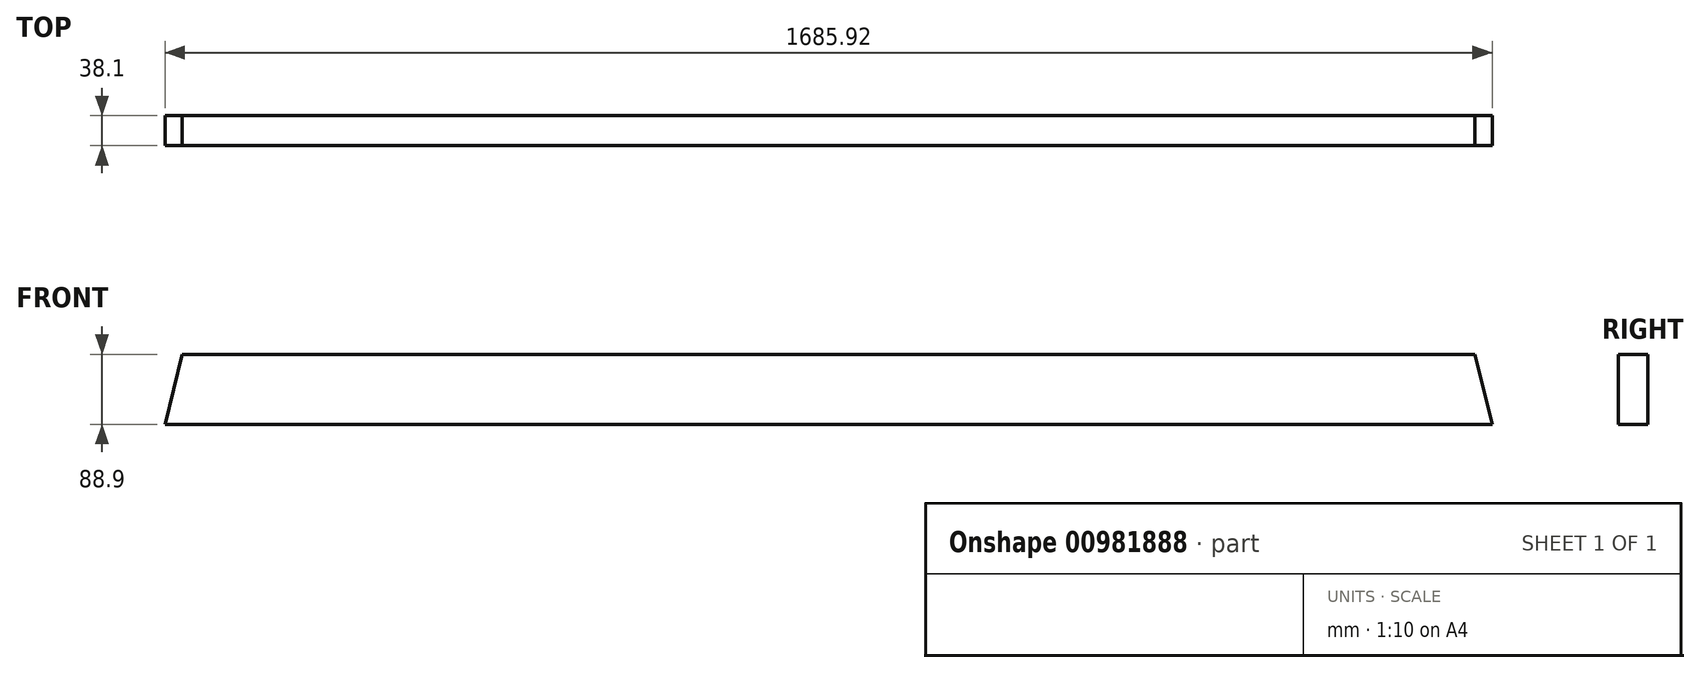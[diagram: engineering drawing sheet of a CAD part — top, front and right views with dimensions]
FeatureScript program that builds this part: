
annotation { "Feature Type Name" : "Feature", "Feature Type Description" : "" }
export const myFeature = defineFeature(function(context is Context, id is Id, definition is map)
    precondition{}
    {
        {
            var Q0;
            Q0=qCreatedBy(makeId("Right.planeOp"),FACE);
            var sketch = newSketch(context, id + "F0", { "sketchPlane" : qUnion([Q0])});
            skLineSegment(sketch, "E0.bottom", {"start": v(-19.05, -44.45) * mm, "end": v(19.05, -44.45) * mm});
            skLineSegment(sketch, "E0.top", {"start": v(-19.05, 44.45) * mm, "end": v(19.05, 44.45) * mm});
            skLineSegment(sketch, "E0.left", {"start": v(-19.05, -44.45) * mm, "end": v(-19.05, 44.45) * mm});
            skLineSegment(sketch, "E0.right", {"start": v(19.05, -44.45) * mm, "end": v(19.05, 44.45) * mm});
            skPoint(sketch, "E0.middle", {"position": v(0, 0) * mm});
            skSolve(sketch);
        }
        {
            var Q0;
            Q0=makeQuery(id+"F0.imprint","IMPRINT",FACE,{"disambiguationData":[TD([[makeQuery(id+"F0.imprint","IMPRINT",EDGE,{"derivedFrom":sQuery(id+"F0.wireOp",EDGE,"E0.bottom")}),1.0]])]});
            extrude(context, id + "F1", {"entities" : qUnion([Q0]), "endBound" : BoundingType.SYMMETRIC, "depth" : 1685.92 * mm, "offsetDistance" : 25.4 * mm});
        }
        {
            var Q0;
            Q0=makeQuery(id+"F1.opExtrude","CAP_EDGE",EDGE,{"disambiguationData":[OSD([sQuery(id+"F0.wireOp",EDGE,"E0.top")])],"isStart":false});
            var Q1;
            Q1=makeQuery(id+"F1.opExtrude","CAP_EDGE",EDGE,{"disambiguationData":[OSD([sQuery(id+"F0.wireOp",EDGE,"E0.top")])],"isStart":true});
            chamfer(context, id + "F2", {"entities" : qUnion([Q0, Q1]), "chamferType" : ChamferType.TWO_OFFSETS, "width1" : 22.22 * mm, "oppositeDirection" : false, "width2" : 88.9 * mm, "tangentPropagation" : true});
        }
    });
